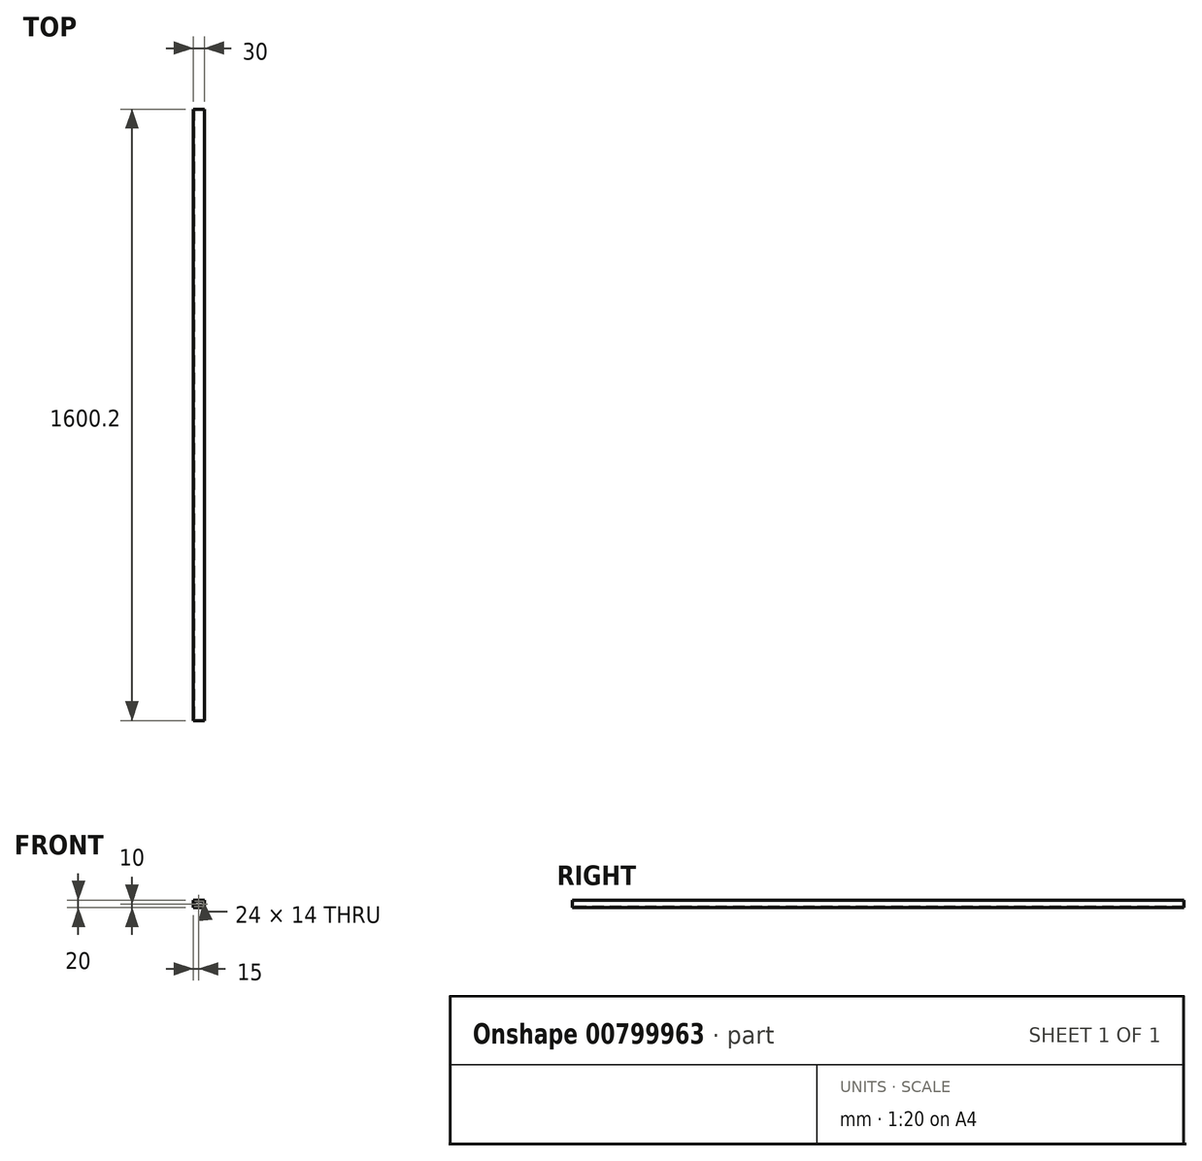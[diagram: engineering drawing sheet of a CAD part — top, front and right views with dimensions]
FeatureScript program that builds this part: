
annotation { "Feature Type Name" : "Feature", "Feature Type Description" : "" }
export const myFeature = defineFeature(function(context is Context, id is Id, definition is map)
    precondition{}
    {
        {
            var Q0;
            Q0=qCreatedBy(makeId("Front.planeOp"),FACE);
            var sketch = newSketch(context, id + "F0", { "sketchPlane" : qUnion([Q0])});
            skLineSegment(sketch, "E0.bottom", {"start": v(0, 0) * mm, "end": v(30, 0) * mm});
            skLineSegment(sketch, "E0.top", {"start": v(0, 20) * mm, "end": v(30, 20) * mm});
            skLineSegment(sketch, "E0.left", {"start": v(0, 0) * mm, "end": v(0, 20) * mm});
            skLineSegment(sketch, "E0.right", {"start": v(30, 0) * mm, "end": v(30, 20) * mm});
            skSolve(sketch);
        }
        {
            var Q0;
            Q0 = qSketchRegion(id + "F0", true);
            extrude(context, id + "F1", {"entities" : qUnion([Q0]), "depth" : 1600.2 * mm, "offsetDistance" : 25 * mm});
        }
        {
            var Q0;
            Q0=makeQuery(id+"F1.opExtrude","CAP_FACE",FACE,{"disambiguationData":[OSD([sQuery(id+"F0.wireOp",EDGE,"E0.bottom"),sQuery(id+"F0.wireOp",EDGE,"E0.top"),sQuery(id+"F0.wireOp",EDGE,"E0.left"),sQuery(id+"F0.wireOp",EDGE,"E0.right")])],"isStart":false});
            var sketch = newSketch(context, id + "F2", { "sketchPlane" : qUnion([Q0])});
            skLineSegment(sketch, "E1.0", {"start": v(27, 17) * mm, "end": v(3, 17) * mm});
            skLineSegment(sketch, "E1.1", {"start": v(27, 3) * mm, "end": v(27, 17) * mm});
            skLineSegment(sketch, "E1.2", {"start": v(3, 3) * mm, "end": v(27, 3) * mm});
            skLineSegment(sketch, "E1.3", {"start": v(3, 17) * mm, "end": v(3, 3) * mm});
            skSolve(sketch);
        }
        {
            var Q0;
            Q0 = qSketchRegion(id + "F2", true);
            extrude(context, id + "F3", {"entities" : qUnion([Q0]), "operationType" : NewBodyOperationType.REMOVE, "endBound" : BoundingType.THROUGH_ALL, "oppositeDirection" : true, "depth" : 25 * mm, "offsetDistance" : 25 * mm});
        }
    });
